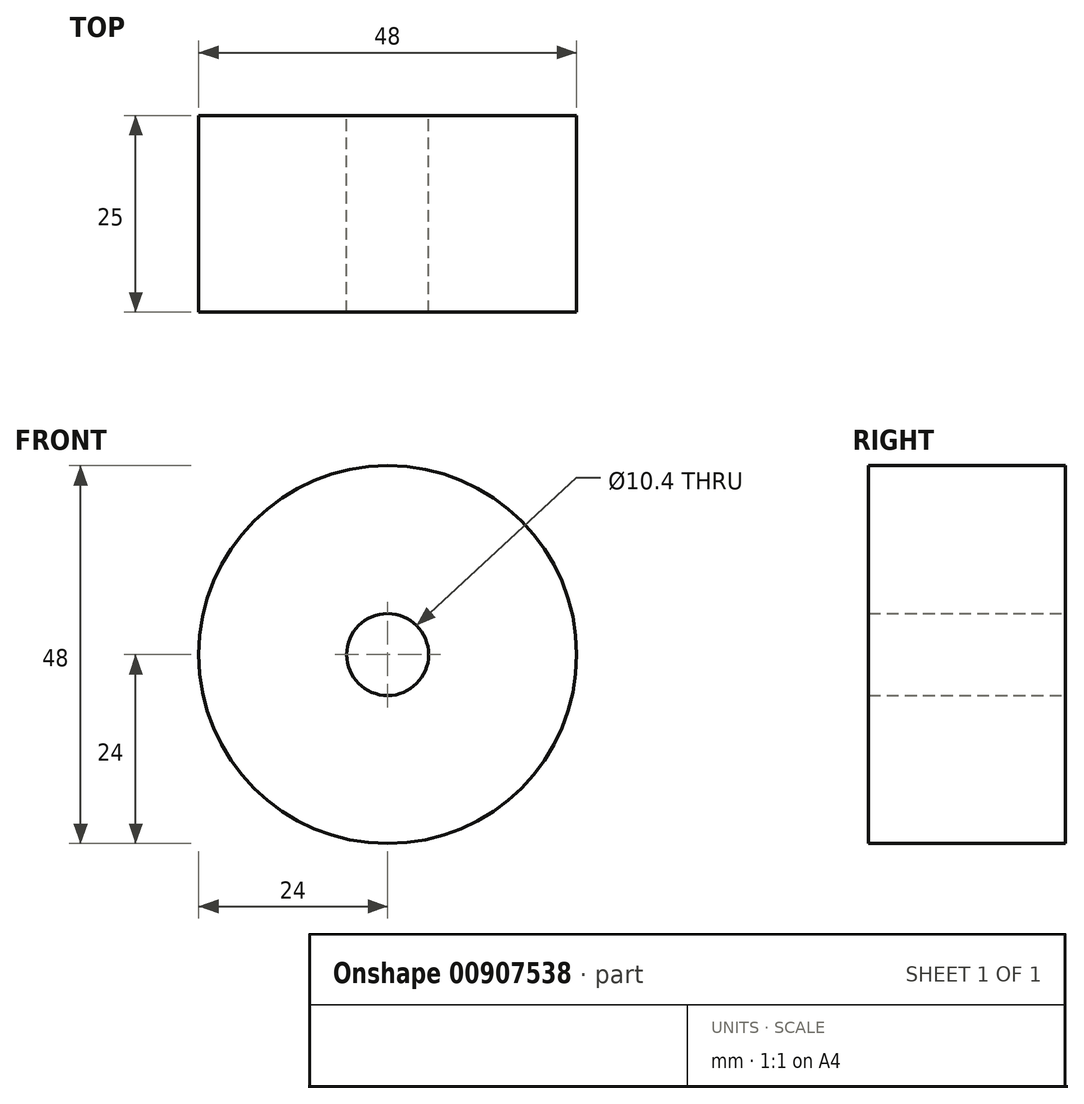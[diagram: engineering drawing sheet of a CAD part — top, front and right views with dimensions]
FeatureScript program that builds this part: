
annotation { "Feature Type Name" : "Feature", "Feature Type Description" : "" }
export const myFeature = defineFeature(function(context is Context, id is Id, definition is map)
    precondition{}
    {
        {
            var Q0;
            Q0=qCreatedBy(makeId("Front.planeOp"),FACE);
            var sketch = newSketch(context, id + "F0", { "sketchPlane" : qUnion([Q0])});
            skCircle(sketch, "E0", {"center": v(0, 0) * mm, "radius": 24 * mm});
            skCircle(sketch, "E1", {"center": v(0, 0) * mm, "radius": 5.2 * mm});
            skSolve(sketch);
        }
        {
            var Q0;
            Q0 = qSketchRegion(id + "F0", true);
            var Q1;
            Q1=makeQuery(id+"F0.imprint","IMPRINT",FACE,{"disambiguationData":[TD([[makeQuery(id+"F0.imprint","IMPRINT",EDGE,{"derivedFrom":sQuery(id+"F0.wireOp",EDGE,"E0")}),1.0]])]});
            extrude(context, id + "F1", {"entities" : qUnion([Q0, Q1]), "depth" : 25 * mm, "offsetDistance" : 25 * mm});
        }
    });
